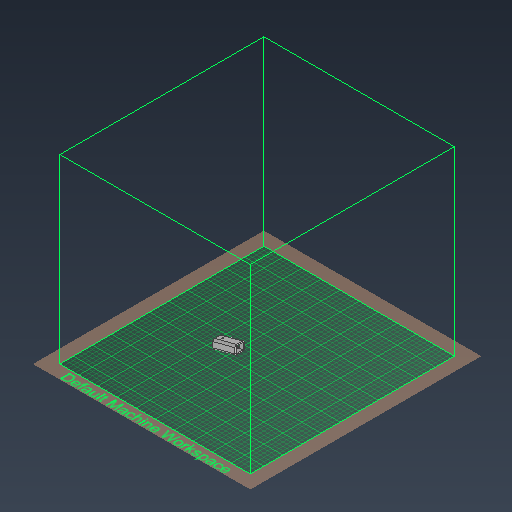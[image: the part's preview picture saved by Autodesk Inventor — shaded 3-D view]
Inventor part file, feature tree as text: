
AUTODESK INVENTOR PART (.ipt)
format: ipt  version: 2021 (Build 250183000, 183)  size: 364,032 bytes
history: native  units: mm
features: sketch x6, extrude x6, fillet x2, plane x1, shell x1
ambient origin geometry x8: Origin, YZ Plane, XZ Plane, XY Plane, X Axis, Y Axis, Z Axis, Center Point
bodies: Volumenkörper1 (feature_tree)
feature tree (16):
  sketch  "Skizze1"  dims[d0=17.434mm d1=110.0mm]
  plane  "Arbeitsebene2"
  extrude  "Extrusion2"  Depth=110.0mm
  extrude  "Extrusion4"  Depth=20.0mm
  extrude  "Extrusion5"  Depth=14.4mm
  shell  "Wandung2"  Thickness=2.0mm
  fillet  "Rundung5"  Radius=3.2mm
  extrude  "Extrusion6"  TaperAngle=0.0deg  [1 undecoded]
  fillet  "Rundung6"  Radius=10.0mm
  extrude  "Extrusion7"  Depth=20.0mm
  extrude  "Extrusion8"  Depth=20.0mm
  sketch  "Skizze3"  dims[d4=20.0mm d5=11.128mm]
  sketch  "Skizze5"  dims[d13=14.4mm d14=14.4mm d15=2.0mm]
  sketch  "Skizze6"  dims[d16=15.0mm d17=7.5mm d18=0.0mm d19=0.0mm d29=3.2mm]
  sketch  "Skizze7"  dims[d31=0.0mm d32=0.0mm d34=10.0mm d35=0.0mm]
  sketch  "Skizze8"  dims[d38=4.706446mm d39=16.495633mm d40=3.490659mm d42=20.0mm d43=0.0mm d44=28.012412mm d45=2.6mm d46=4.0mm d47=7.2mm d48=9.0mm d49=12.0mm d50=12.0mm d51=4.0mm d52=19.0mm d53=3.0mm d54=0.0mm d55=2.0mm d56=3.490659mm d57=3.2mm d58=8.0mm d59=3.0mm d60=0.0mm d61=20.0mm d62=0.0mm]
note: 1 required parameter value undecoded (feature->parameter linkage not recoverable at this tier; creation-order binding heuristic only, values carry confidence <= 0.55)
